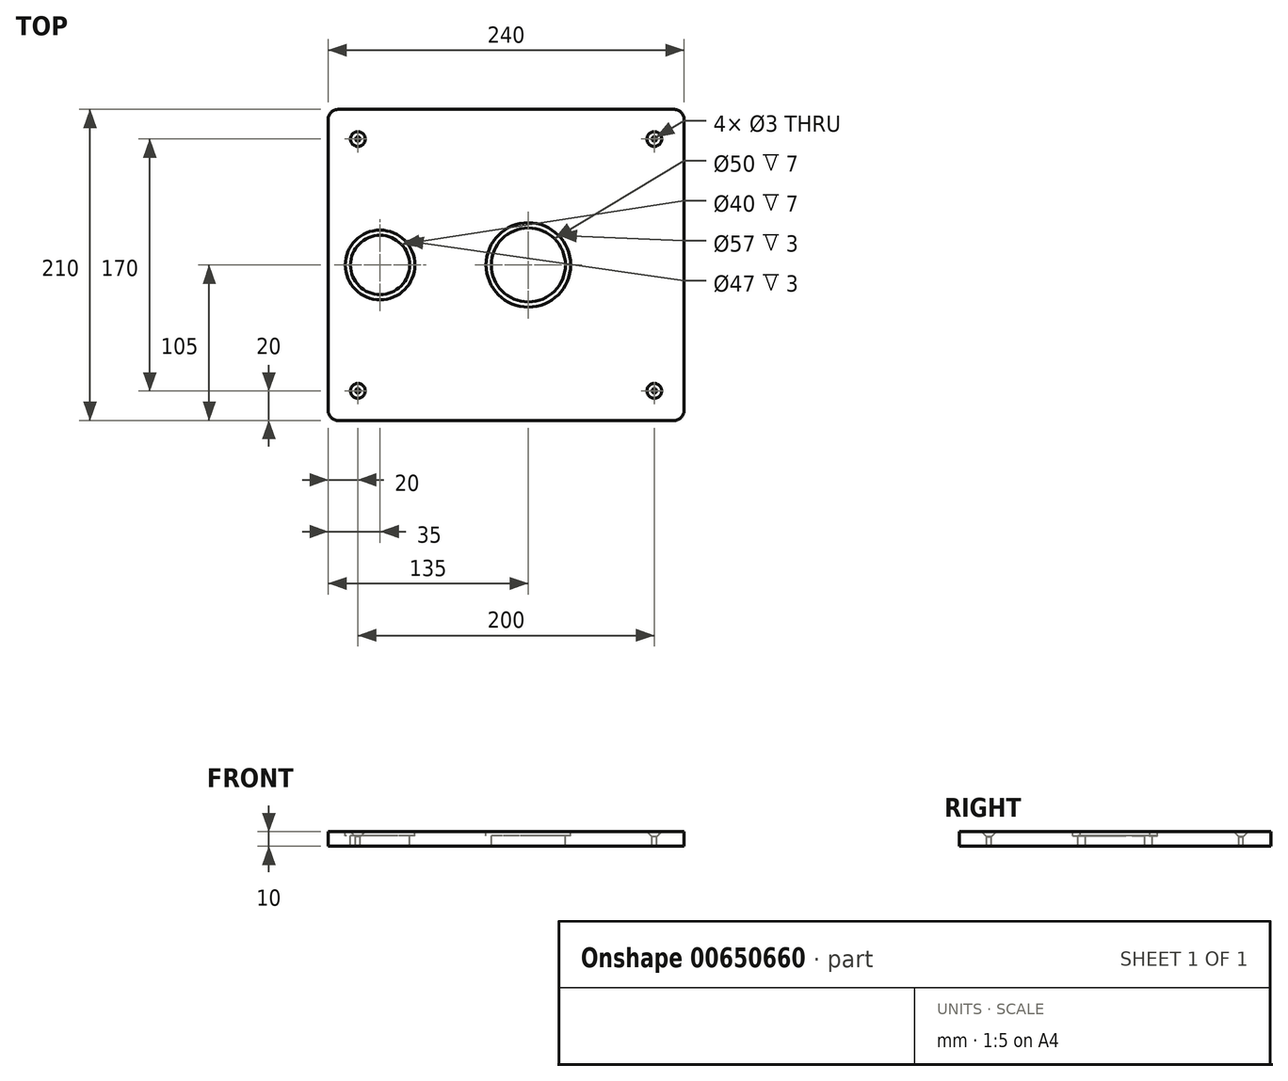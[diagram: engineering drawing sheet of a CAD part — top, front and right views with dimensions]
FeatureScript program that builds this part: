
annotation { "Feature Type Name" : "Feature", "Feature Type Description" : "" }
export const myFeature = defineFeature(function(context is Context, id is Id, definition is map)
    precondition{}
    {
        {
            var Q0;
            Q0=qCreatedBy(makeId("Top.planeOp"),FACE);
            var sketch = newSketch(context, id + "F0", { "sketchPlane" : qUnion([Q0])});
            skLineSegment(sketch, "E0.bottom", {"start": v(-128.5, 105) * mm, "end": v(98.5, 105) * mm});
            skLineSegment(sketch, "E0.top", {"start": v(-128.5, -105) * mm, "end": v(98.5, -105) * mm});
            skLineSegment(sketch, "E0.left", {"start": v(-135, 98.5) * mm, "end": v(-135, -98.5) * mm});
            skLineSegment(sketch, "E0.right", {"start": v(105, 98.5) * mm, "end": v(105, -98.5) * mm});
            skCircle(sketch, "E1", {"center": v(0, 0) * mm, "radius": 25 * mm});
            skCircle(sketch, "E2", {"center": v(-100, 0) * mm, "radius": 20 * mm});
            skPoint(sketch, "E3.visualSharp", {"position": v(-135, 105) * mm});
            skArc(sketch, "E3.filletArc", {"start": v(-128.5, 105) * mm, "mid": v(-133.1, 103.1) * mm, "end": v(-135, 98.5) * mm});
            skPoint(sketch, "E4.visualSharp", {"position": v(105, 105) * mm});
            skArc(sketch, "E4.filletArc", {"start": v(105, 98.5) * mm, "mid": v(103.1, 103.1) * mm, "end": v(98.5, 105) * mm});
            skPoint(sketch, "E5.visualSharp", {"position": v(105, -105) * mm});
            skArc(sketch, "E5.filletArc", {"start": v(98.5, -105) * mm, "mid": v(103.1, -103.1) * mm, "end": v(105, -98.5) * mm});
            skPoint(sketch, "E6.visualSharp", {"position": v(-135, -105) * mm});
            skArc(sketch, "E6.filletArc", {"start": v(-135, -98.5) * mm, "mid": v(-133.1, -103.1) * mm, "end": v(-128.5, -105) * mm});
            skLineSegment(sketch, "E7", {"start": v(-15, -105) * mm, "end": v(-15, 105) * mm, "construction": true});
            skPoint(sketch, "E8", {"position": v(85, 85) * mm});
            skPoint(sketch, "E9", {"position": v(-115, 85) * mm});
            skPoint(sketch, "E10", {"position": v(85, -85) * mm});
            skPoint(sketch, "E11", {"position": v(-115, -85) * mm});
            skSolve(sketch);
        }
        {
            var Q0;
            Q0=makeQuery(id+"F0.imprint","IMPRINT",FACE,{"disambiguationData":[TD([[makeQuery(id+"F0.imprint","IMPRINT",EDGE,{"derivedFrom":sQuery(id+"F0.wireOp",EDGE,"E0.bottom")}),-1.0]])]});
            extrude(context, id + "F1", {"entities" : qUnion([Q0]), "oppositeDirection" : true, "depth" : 10 * mm, "offsetDistance" : 25 * mm});
        }
        {
            var Q0;
            Q0=makeQuery(id+"F1.opExtrude","CAP_FACE",FACE,{"disambiguationData":[OSD([sQuery(id+"F0.wireOp",EDGE,"E0.bottom"),sQuery(id+"F0.wireOp",EDGE,"E0.top"),sQuery(id+"F0.wireOp",EDGE,"E0.left"),sQuery(id+"F0.wireOp",EDGE,"E0.right"),sQuery(id+"F0.wireOp",EDGE,"E1"),sQuery(id+"F0.wireOp",EDGE,"E2"),sQuery(id+"F0.wireOp",EDGE,"E3.filletArc"),sQuery(id+"F0.wireOp",EDGE,"E4.filletArc"),sQuery(id+"F0.wireOp",EDGE,"E5.filletArc"),sQuery(id+"F0.wireOp",EDGE,"E6.filletArc")])],"isStart":true});
            var sketch = newSketch(context, id + "F2", { "sketchPlane" : qUnion([Q0])});
            skCircle(sketch, "E12.0", {"center": v(-100, 0) * mm, "radius": 23.5 * mm});
            skCircle(sketch, "E13.0", {"center": v(0, 0) * mm, "radius": 28.5 * mm});
            skSolve(sketch);
        }
        {
            var Q0;
            Q0=makeQuery(id+"F2.imprint","IMPRINT",FACE,{"disambiguationData":[TD([[makeQuery(id+"F2.imprint","IMPRINT",EDGE,{"derivedFrom":sQuery(id+"F2.wireOp",EDGE,"E12.0")}),1.0]])]});
            var Q1;
            Q1=makeQuery(id+"F2.imprint","IMPRINT",FACE,{"disambiguationData":[TD([[makeQuery(id+"F2.imprint","IMPRINT",EDGE,{"derivedFrom":sQuery(id+"F2.wireOp",EDGE,"E13.0")}),1.0]])]});
            extrude(context, id + "F3", {"entities" : qUnion([Q0, Q1]), "operationType" : NewBodyOperationType.REMOVE, "oppositeDirection" : true, "depth" : 3 * mm, "offsetDistance" : 25 * mm});
        }
        {
            var Q0;
            Q0=sQuery(id+"F0.wireOp",VERTEX,"E9");
            var Q1;
            Q1=sQuery(id+"F0.wireOp",VERTEX,"E8");
            var Q2;
            Q2=sQuery(id+"F0.wireOp",VERTEX,"E10");
            var Q3;
            Q3=sQuery(id+"F0.wireOp",VERTEX,"E11");
            var Q4;
            Q4=makeQuery(id+"F1.opExtrude","SWEPT_BODY",BODY,{"disambiguationData":[OSD([sQuery(id+"F0.wireOp",EDGE,"E0.bottom"),sQuery(id+"F0.wireOp",EDGE,"E0.top"),sQuery(id+"F0.wireOp",EDGE,"E0.left"),sQuery(id+"F0.wireOp",EDGE,"E0.right"),sQuery(id+"F0.wireOp",EDGE,"E1"),sQuery(id+"F0.wireOp",EDGE,"E2"),sQuery(id+"F0.wireOp",EDGE,"E3.filletArc"),sQuery(id+"F0.wireOp",EDGE,"E4.filletArc"),sQuery(id+"F0.wireOp",EDGE,"E5.filletArc"),sQuery(id+"F0.wireOp",EDGE,"E6.filletArc")])]});
            hole(context, id + "F4", {"style" : HoleStyle.C_SINK, "endStyle" : HoleEndStyle.THROUGH, "holeDiameter" : 3 * mm, "cSinkDiameter" : 10 * mm, "cSinkAngle" : 90 * degree, "majorDiameter" : 5 * mm, "isTappedThrough" : true, "tappedDepth" : 12 * mm, "tapClearance" : 3, "locations" : qUnion([Q0, Q1, Q2, Q3]), "scope" : qUnion([Q4])});
        }
    });
